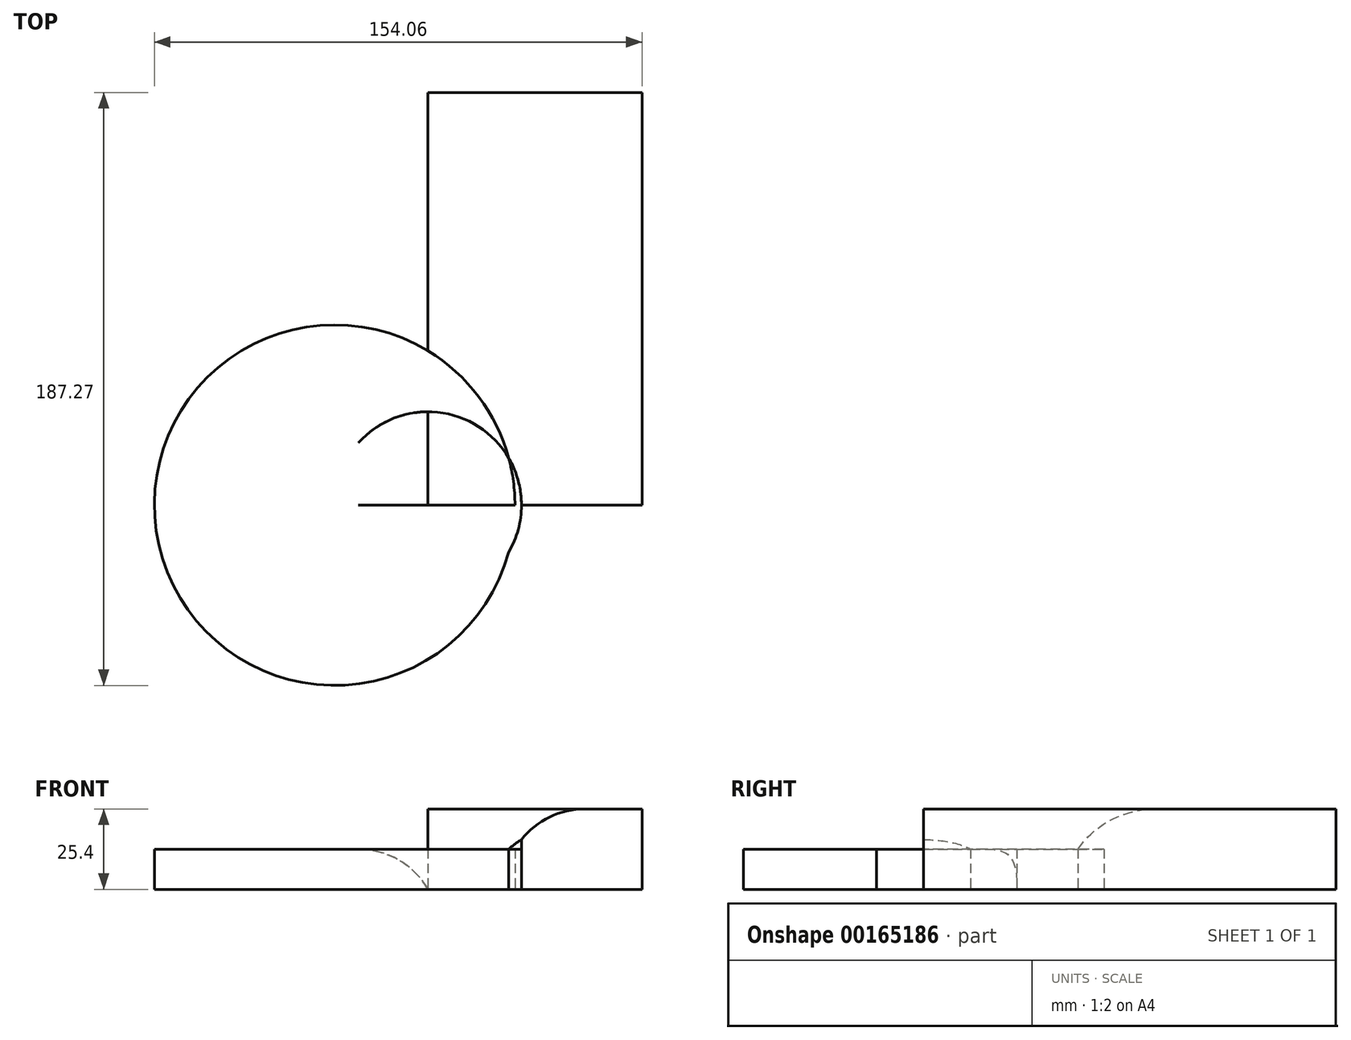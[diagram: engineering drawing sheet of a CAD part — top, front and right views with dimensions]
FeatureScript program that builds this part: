
annotation { "Feature Type Name" : "Feature", "Feature Type Description" : "" }
export const myFeature = defineFeature(function(context is Context, id is Id, definition is map)
    precondition{}
    {
        {
            var Q0;
            Q0=qCreatedBy(makeId("Top.planeOp"),FACE);
            var sketch = newSketch(context, id + "F0", { "sketchPlane" : qUnion([Q0])});
            skLineSegment(sketch, "E0.bottom", {"start": v(-70.15, 0) * mm, "end": v(-2.55, 0) * mm});
            skLineSegment(sketch, "E0.top", {"start": v(-70.15, 130.3) * mm, "end": v(-2.55, 130.3) * mm});
            skLineSegment(sketch, "E0.left", {"start": v(-70.15, 0) * mm, "end": v(-70.15, 130.3) * mm});
            skLineSegment(sketch, "E0.right", {"start": v(-2.55, 0) * mm, "end": v(-2.55, 130.3) * mm});
            skPoint(sketch, "E0.middle", {"position": v(-36.35, 65.15) * mm});
            skLineSegment(sketch, "E1.bottom", {"start": v(-2.55, 130.3) * mm, "end": v(-42.7, 130.3) * mm, "construction": true});
            skLineSegment(sketch, "E1.top", {"start": v(-2.55, -64.47) * mm, "end": v(-42.7, -64.47) * mm, "construction": true});
            skLineSegment(sketch, "E1.left", {"start": v(-2.55, 130.3) * mm, "end": v(-2.55, -64.47) * mm, "construction": true});
            skLineSegment(sketch, "E1.right", {"start": v(-42.7, 130.3) * mm, "end": v(-42.7, -64.47) * mm, "construction": true});
            skPoint(sketch, "E1.middle", {"position": v(-22.62, 32.92) * mm});
            skCircle(sketch, "E2", {"center": v(-70.15, 0) * mm, "radius": 29.5 * mm});
            skCircle(sketch, "E3", {"center": v(-99.65, 0) * mm, "radius": 56.96 * mm});
            skSolve(sketch);
        }
        {
            var Q0;
            {var subQ2=sQuery(id+"F0.wireOp",EDGE,"E0.top");Q0=makeQuery(id+"F0.imprint","IMPRINT",FACE,{"disambiguationData":[TD([[makeQuery(id+"F0.imprint","IMPRINT",EDGE,{"derivedFrom":subQ2}),-1.0]])]});}
            extrude(context, id + "F1", {"entities" : qUnion([Q0]), "depth" : 25.4 * mm});
        }
        {
            var Q0;
            Q0 = qSketchRegion(id + "F0", true);
            extrude(context, id + "F2", {"entities" : qUnion([Q0]), "operationType" : NewBodyOperationType.ADD, "depth" : 12.7 * mm});
        }
        {
            var Q0;
            {var subQ0=sQuery(id+"F0.wireOp",EDGE,"E0.left");Q0=makeQuery(id+"F2.opExtrude","CAP_EDGE",EDGE,{"disambiguationData":[OSD([subQ0]),TDD([makeQuery(id+"F0.imprint","IMPRINT",EDGE,{"disambiguationData":[TD([[makeQuery(id+"F0.imprint","INTERSECT",VERTEX,{"derivedFrom":[sQuery(id+"F0.wireOp",EDGE,"E0.bottom"),subQ0]}),-1.0]])],"derivedFrom":subQ0})])],"isStart":false});}
            var Q1;
            Q1=makeQuery(id+"F1.opExtrude","CAP_EDGE",EDGE,{"disambiguationData":[OSD([sQuery(id+"F0.wireOp",EDGE,"E3")])],"isStart":false});
            fillet(context, id + "F3", {"entities" : qUnion([Q0, Q1]), "radius" : 25.4 * mm, "tangentPropagation" : true, "allowEdgeOverflow" : false});
        }
    });
